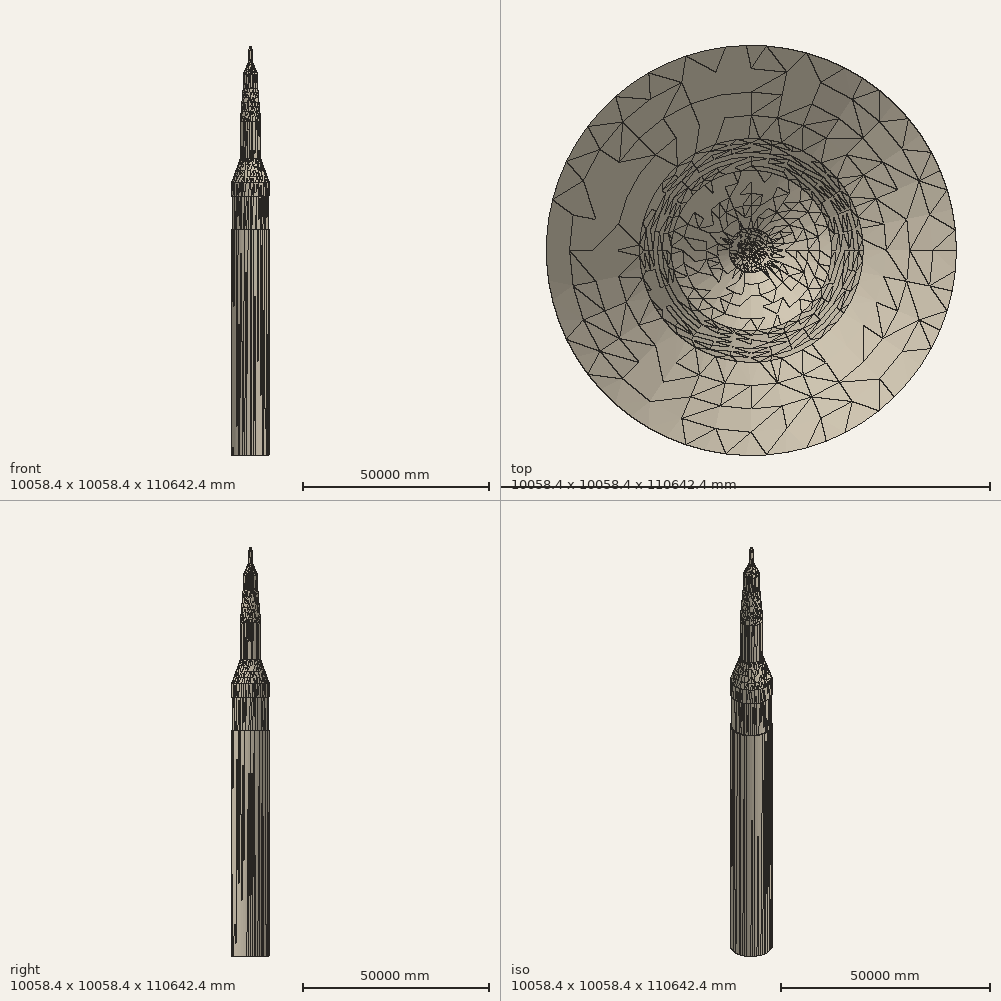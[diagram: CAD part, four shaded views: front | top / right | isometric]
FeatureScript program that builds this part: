
annotation { "Feature Type Name" : "Feature", "Feature Type Description" : "" }
export const myFeature = defineFeature(function(context is Context, id is Id, definition is map)
    precondition{}
    {
        {
            var Q0;
            Q0=qCreatedBy(makeId("Front.planeOp"),FACE);
            var sketch = newSketch(context, id + "F0", { "sketchPlane" : qUnion([Q0])});
            skLineSegment(sketch, "E0", {"start": v(0, 49580.8) * mm, "end": v(0, -61061.6) * mm});
            skLineSegment(sketch, "E1", {"start": v(0, -61061.6) * mm, "end": v(5029.2, -61061.6) * mm});
            skLineSegment(sketch, "E2", {"start": v(5029.2, -61061.6) * mm, "end": v(5029.2, 12700) * mm});
            skLineSegment(sketch, "E3", {"start": v(5029.2, 12700) * mm, "end": v(2743.2, 18980.73) * mm});
            skLineSegment(sketch, "E4", {"start": v(2743.2, 18980.73) * mm, "end": v(2743.2, 29178.83) * mm});
            skLineSegment(sketch, "E5", {"start": v(2743.2, 29178.83) * mm, "end": v(1965.43, 38068.83) * mm});
            skLineSegment(sketch, "E6", {"start": v(1965.43, 38068.83) * mm, "end": v(1965.43, 41878.83) * mm});
            skLineSegment(sketch, "E7", {"start": v(1965.43, 41878.83) * mm, "end": v(544.12, 44926.83) * mm});
            skLineSegment(sketch, "E8", {"start": v(544.12, 44926.83) * mm, "end": v(544.12, 48101.83) * mm});
            skLineSegment(sketch, "E9", {"start": v(544.12, 48101.83) * mm, "end": v(0, 49580.8) * mm});
            skLineSegment(sketch, "E10", {"start": v(5029.2, 8890) * mm, "end": v(4775.2, 8890) * mm});
            skLineSegment(sketch, "E11", {"start": v(4775.2, 8890) * mm, "end": v(4775.2, 0) * mm});
            skLineSegment(sketch, "E12", {"start": v(4775.2, 0) * mm, "end": v(5029.2, 0) * mm});
            skSolve(sketch);
        }
        {
            var Q0;
            Q0=makeQuery(id+"F0.imprint","IMPRINT",FACE,{"disambiguationData":[TD([[makeQuery(id+"F0.imprint","IMPRINT",EDGE,{"derivedFrom":sQuery(id+"F0.wireOp",EDGE,"E0")}),1.0]])]});
            var Q1;
            Q1=sQuery(id+"F0.wireOp",EDGE,"E0");
            revolve(context, id + "F1", {"entities" : qUnion([Q0]), "axis" : qUnion([Q1]), "revolveType" : RevolveType.FULL});
        }
    });
